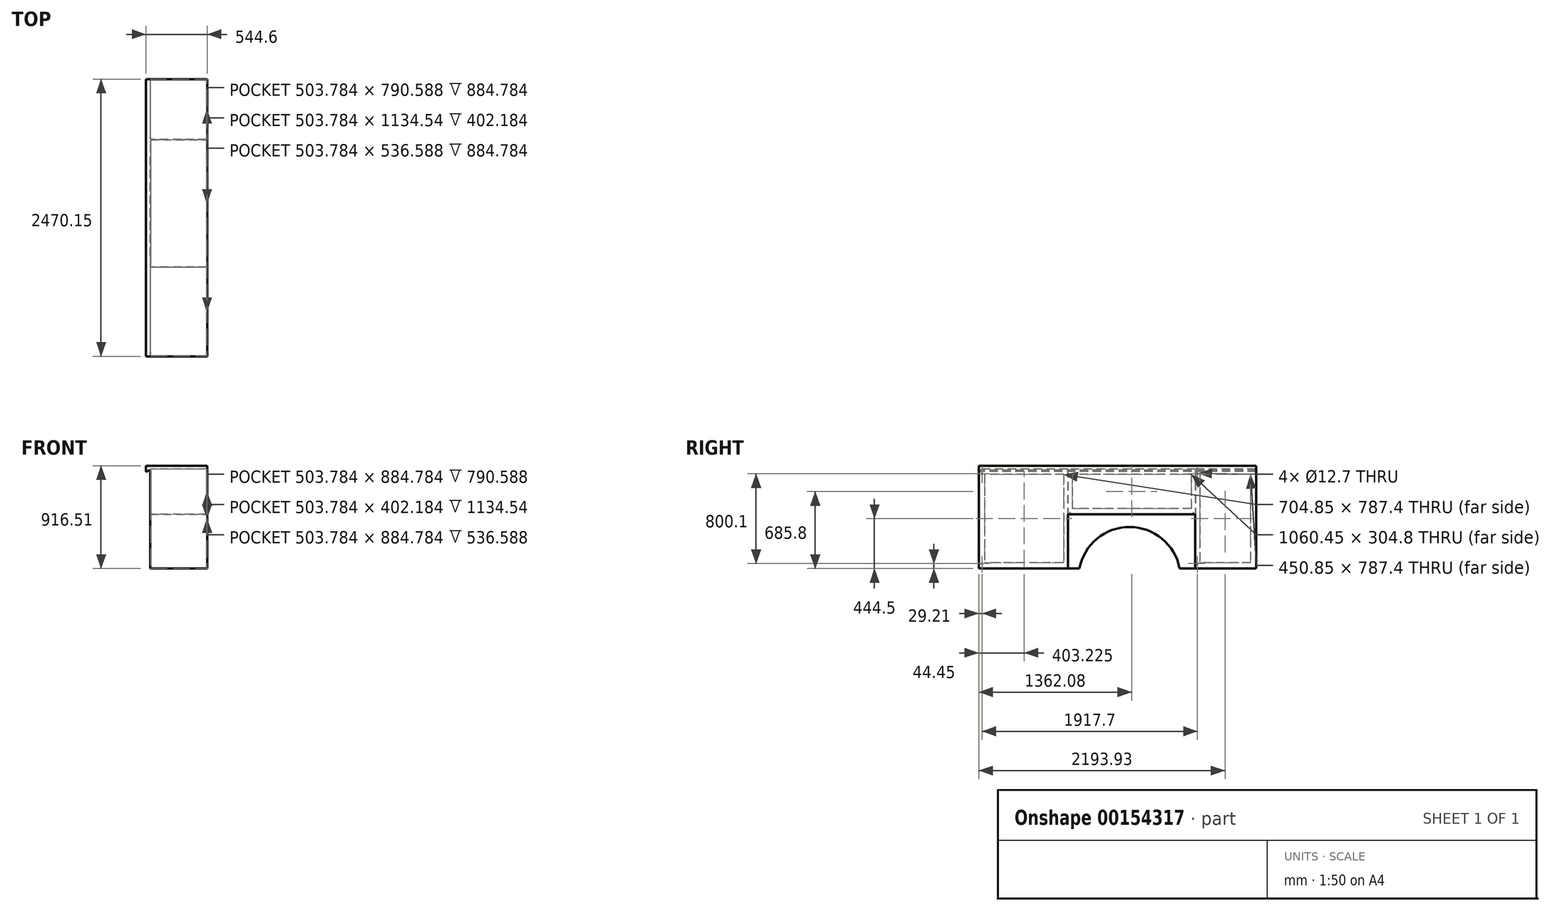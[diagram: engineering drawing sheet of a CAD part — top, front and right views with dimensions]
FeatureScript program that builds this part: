
annotation { "Feature Type Name" : "Feature", "Feature Type Description" : "" }
export const myFeature = defineFeature(function(context is Context, id is Id, definition is map)
    precondition{}
    {
        {
            var Q0;
            Q0=qCreatedBy(makeId("Front.planeOp"),FACE);
            var sketch = newSketch(context, id + "F0", { "sketchPlane" : qUnion([Q0])});
            skLineSegment(sketch, "E0.bottom", {"start": v(-254, 457.2) * mm, "end": v(254, 457.2) * mm});
            skLineSegment(sketch, "E0.top", {"start": v(-254, -457.2) * mm, "end": v(254, -457.2) * mm});
            skLineSegment(sketch, "E0.left", {"start": v(-254, 457.2) * mm, "end": v(-254, -457.2) * mm});
            skLineSegment(sketch, "E0.right", {"start": v(254, 457.2) * mm, "end": v(254, -457.2) * mm});
            skPoint(sketch, "E0.middle", {"position": v(0, 0) * mm});
            skSolve(sketch);
        }
        {
            var Q0;
            Q0 = qSketchRegion(id + "F0", true);
            var Q1;
            Q1 = qSketchRegion(id + "F2", true);
            extrude(context, id + "F1", {"entities" : qUnion([Q0, Q1]), "oppositeDirection" : true, "depth" : 2470.15 * mm});
        }
        {
            var Q0;
            Q0=makeQuery(id+"F1.opExtrude","SWEPT_FACE",FACE,{"disambiguationData":[OSD([sQuery(id+"F0.wireOp",EDGE,"E0.left")])]});
            var sketch = newSketch(context, id + "F2", { "sketchPlane" : qUnion([Q0])});
            skLineSegment(sketch, "E1", {"start": v(-1930.4, 457.2) * mm, "end": v(-1930.4, -457.2) * mm});
            skLineSegment(sketch, "E2", {"start": v(-793.75, 457.2) * mm, "end": v(-793.75, -457.2) * mm});
            skLineSegment(sketch, "E3", {"start": v(-1930.4, 25.4) * mm, "end": v(-793.75, 25.4) * mm});
            skLineSegment(sketch, "E4.bottom", {"start": v(-2419.35, 381) * mm, "end": v(-1968.5, 381) * mm});
            skLineSegment(sketch, "E4.top", {"start": v(-2419.35, -406.4) * mm, "end": v(-1968.5, -406.4) * mm});
            skLineSegment(sketch, "E4.left", {"start": v(-2419.35, 381) * mm, "end": v(-2419.35, -406.4) * mm});
            skLineSegment(sketch, "E4.right", {"start": v(-1968.5, 381) * mm, "end": v(-1968.5, -406.4) * mm});
            skLineSegment(sketch, "E5.bottom", {"start": v(-1892.3, 381) * mm, "end": v(-831.85, 381) * mm});
            skLineSegment(sketch, "E5.top", {"start": v(-1892.3, 76.2) * mm, "end": v(-831.85, 76.2) * mm});
            skLineSegment(sketch, "E5.left", {"start": v(-1892.3, 381) * mm, "end": v(-1892.3, 76.2) * mm});
            skLineSegment(sketch, "E5.right", {"start": v(-831.85, 381) * mm, "end": v(-831.85, 76.2) * mm});
            skLineSegment(sketch, "E6.bottom", {"start": v(-755.65, 381) * mm, "end": v(-50.8, 381) * mm});
            skLineSegment(sketch, "E6.top", {"start": v(-755.65, -406.4) * mm, "end": v(-50.8, -406.4) * mm});
            skLineSegment(sketch, "E6.left", {"start": v(-755.65, 381) * mm, "end": v(-755.65, -406.4) * mm});
            skLineSegment(sketch, "E6.right", {"start": v(-50.8, 381) * mm, "end": v(-50.8, -406.4) * mm});
            skSolve(sketch);
        }
        {
            var Q0;
            Q0 = qSketchRegion(id + "F2", true);
            extrude(context, id + "F3", {"entities" : qUnion([Q0]), "operationType" : NewBodyOperationType.REMOVE, "oppositeDirection" : true, "depth" : 505.9 * mm});
        }
        {
            var Q0;
            Q0=makeQuery(id+"F3.boolean.opBoolean","COPY",FACE,{"derivedFrom":makeQuery(id+"F3.opExtrude","SWEPT_FACE",FACE,{"disambiguationData":[OSD([sQuery(id+"F2.wireOp",EDGE,"E6.top")])]})});
            var sketch = newSketch(context, id + "F4", { "sketchPlane" : qUnion([Q0])});
            skLineSegment(sketch, "E7.bottom", {"start": v(251.9, 50.8) * mm, "end": v(-251.9, 50.8) * mm});
            skLineSegment(sketch, "E7.top", {"start": v(251.9, 755.65) * mm, "end": v(-251.9, 755.65) * mm});
            skLineSegment(sketch, "E7.left", {"start": v(251.9, 50.8) * mm, "end": v(251.9, 755.65) * mm});
            skLineSegment(sketch, "E7.right", {"start": v(-251.9, 50.8) * mm, "end": v(-251.9, 755.65) * mm});
            skSolve(sketch);
        }
        {
            var Q0;
            Q0 = qSketchRegion(id + "F4", true);
            extrude(context, id + "F5", {"entities" : qUnion([Q0]), "operationType" : NewBodyOperationType.REMOVE, "oppositeDirection" : true, "depth" : 48.7 * mm});
        }
        {
            var Q0;
            Q0=makeQuery(id+"F3.boolean.opBoolean","COPY",FACE,{"derivedFrom":makeQuery(id+"F3.opExtrude","SWEPT_FACE",FACE,{"disambiguationData":[OSD([sQuery(id+"F2.wireOp",EDGE,"E6.bottom")])]})});
            var sketch = newSketch(context, id + "F6", { "sketchPlane" : qUnion([Q0])});
            skLineSegment(sketch, "E8.bottom", {"start": v(251.9, -50.8) * mm, "end": v(-251.9, -50.8) * mm});
            skLineSegment(sketch, "E8.top", {"start": v(251.9, -755.65) * mm, "end": v(-251.9, -755.65) * mm});
            skLineSegment(sketch, "E8.left", {"start": v(251.9, -50.8) * mm, "end": v(251.9, -755.65) * mm});
            skLineSegment(sketch, "E8.right", {"start": v(-251.9, -50.8) * mm, "end": v(-251.9, -755.65) * mm});
            skSolve(sketch);
        }
        {
            var Q0;
            Q0 = qSketchRegion(id + "F6", true);
            extrude(context, id + "F7", {"entities" : qUnion([Q0]), "operationType" : NewBodyOperationType.REMOVE, "oppositeDirection" : true, "depth" : 48.7 * mm});
        }
        {
            var Q0;
            Q0=makeQuery(id+"F7.boolean.opBoolean","MERGE",FACE,{"derivedFrom":[makeQuery(id+"F5.boolean.opBoolean","MERGE",FACE,{"derivedFrom":[makeQuery(id+"F3.boolean.opBoolean","COPY",FACE,{"derivedFrom":makeQuery(id+"F3.opExtrude","SWEPT_FACE",FACE,{"disambiguationData":[OSD([sQuery(id+"F2.wireOp",EDGE,"E6.left")])]})}),makeQuery(id+"F5.opExtrude","SWEPT_FACE",FACE,{"disambiguationData":[OSD([sQuery(id+"F4.wireOp",EDGE,"E7.top")])]})]}),makeQuery(id+"F7.opExtrude","SWEPT_FACE",FACE,{"disambiguationData":[OSD([sQuery(id+"F6.wireOp",EDGE,"E8.top")])]})]});
            var sketch = newSketch(context, id + "F8", { "sketchPlane" : qUnion([Q0])});
            skLineSegment(sketch, "E9.bottom", {"start": v(251.9, 429.7) * mm, "end": v(-251.9, 429.7) * mm});
            skLineSegment(sketch, "E9.top", {"start": v(251.9, -455.1) * mm, "end": v(-251.9, -455.1) * mm});
            skLineSegment(sketch, "E9.left", {"start": v(251.9, 429.7) * mm, "end": v(251.9, -455.1) * mm});
            skLineSegment(sketch, "E9.right", {"start": v(-251.9, 429.7) * mm, "end": v(-251.9, -455.1) * mm});
            skSolve(sketch);
        }
        {
            var Q0;
            Q0 = qSketchRegion(id + "F8", true);
            extrude(context, id + "F9", {"entities" : qUnion([Q0]), "operationType" : NewBodyOperationType.REMOVE, "oppositeDirection" : true, "depth" : 37.05 * mm});
        }
        {
            var Q0;
            Q0=makeQuery(id+"F7.boolean.opBoolean","MERGE",FACE,{"derivedFrom":[makeQuery(id+"F5.boolean.opBoolean","MERGE",FACE,{"derivedFrom":[makeQuery(id+"F3.boolean.opBoolean","COPY",FACE,{"derivedFrom":makeQuery(id+"F3.opExtrude","SWEPT_FACE",FACE,{"disambiguationData":[OSD([sQuery(id+"F2.wireOp",EDGE,"E6.right")])]})}),makeQuery(id+"F5.opExtrude","SWEPT_FACE",FACE,{"disambiguationData":[OSD([sQuery(id+"F4.wireOp",EDGE,"E7.bottom")])]})]}),makeQuery(id+"F7.opExtrude","SWEPT_FACE",FACE,{"disambiguationData":[OSD([sQuery(id+"F6.wireOp",EDGE,"E8.bottom")])]})]});
            var sketch = newSketch(context, id + "F10", { "sketchPlane" : qUnion([Q0])});
            skLineSegment(sketch, "E10.bottom", {"start": v(-251.9, -455.1) * mm, "end": v(251.9, -455.1) * mm});
            skLineSegment(sketch, "E10.top", {"start": v(-251.9, 429.7) * mm, "end": v(251.9, 429.7) * mm});
            skLineSegment(sketch, "E10.left", {"start": v(-251.9, -455.1) * mm, "end": v(-251.9, 429.7) * mm});
            skLineSegment(sketch, "E10.right", {"start": v(251.9, -455.1) * mm, "end": v(251.9, 429.7) * mm});
            skSolve(sketch);
        }
        {
            var Q0;
            Q0 = qSketchRegion(id + "F10", true);
            extrude(context, id + "F11", {"entities" : qUnion([Q0]), "operationType" : NewBodyOperationType.REMOVE, "oppositeDirection" : true, "depth" : 48.7 * mm});
        }
        {
            var Q0;
            Q0=makeQuery(id+"F3.boolean.opBoolean","COPY",FACE,{"derivedFrom":makeQuery(id+"F3.opExtrude","SWEPT_FACE",FACE,{"disambiguationData":[OSD([sQuery(id+"F2.wireOp",EDGE,"E5.top")])]})});
            var sketch = newSketch(context, id + "F12", { "sketchPlane" : qUnion([Q0])});
            skLineSegment(sketch, "E11.bottom", {"start": v(251.9, 1892.3) * mm, "end": v(-251.9, 1892.3) * mm});
            skLineSegment(sketch, "E11.top", {"start": v(251.9, 831.85) * mm, "end": v(-251.9, 831.85) * mm});
            skLineSegment(sketch, "E11.left", {"start": v(251.9, 1892.3) * mm, "end": v(251.9, 831.85) * mm});
            skLineSegment(sketch, "E11.right", {"start": v(-251.9, 1892.3) * mm, "end": v(-251.9, 831.85) * mm});
            skSolve(sketch);
        }
        {
            var Q0;
            Q0 = qSketchRegion(id + "F12", true);
            extrude(context, id + "F13", {"entities" : qUnion([Q0]), "operationType" : NewBodyOperationType.REMOVE, "oppositeDirection" : true, "depth" : 48.7 * mm});
        }
        {
            var Q0;
            Q0=makeQuery(id+"F3.boolean.opBoolean","COPY",FACE,{"derivedFrom":makeQuery(id+"F3.opExtrude","SWEPT_FACE",FACE,{"disambiguationData":[OSD([sQuery(id+"F2.wireOp",EDGE,"E5.bottom")])]})});
            var sketch = newSketch(context, id + "F14", { "sketchPlane" : qUnion([Q0])});
            skLineSegment(sketch, "E12.bottom", {"start": v(251.9, -1892.3) * mm, "end": v(-251.9, -1892.3) * mm});
            skLineSegment(sketch, "E12.top", {"start": v(251.9, -831.85) * mm, "end": v(-251.9, -831.85) * mm});
            skLineSegment(sketch, "E12.left", {"start": v(251.9, -1892.3) * mm, "end": v(251.9, -831.85) * mm});
            skLineSegment(sketch, "E12.right", {"start": v(-251.9, -1892.3) * mm, "end": v(-251.9, -831.85) * mm});
            skSolve(sketch);
        }
        {
            var Q0;
            Q0 = qSketchRegion(id + "F14", true);
            extrude(context, id + "F15", {"entities" : qUnion([Q0]), "operationType" : NewBodyOperationType.REMOVE, "oppositeDirection" : true, "depth" : 48.7 * mm});
        }
        {
            var Q0;
            Q0=makeQuery(id+"F15.boolean.opBoolean","MERGE",FACE,{"derivedFrom":[makeQuery(id+"F13.boolean.opBoolean","MERGE",FACE,{"derivedFrom":[makeQuery(id+"F3.boolean.opBoolean","COPY",FACE,{"derivedFrom":makeQuery(id+"F3.opExtrude","SWEPT_FACE",FACE,{"disambiguationData":[OSD([sQuery(id+"F2.wireOp",EDGE,"E5.right")])]})}),makeQuery(id+"F13.opExtrude","SWEPT_FACE",FACE,{"disambiguationData":[OSD([sQuery(id+"F12.wireOp",EDGE,"E11.top")])]})]}),makeQuery(id+"F15.opExtrude","SWEPT_FACE",FACE,{"disambiguationData":[OSD([sQuery(id+"F14.wireOp",EDGE,"E12.top")])]})]});
            var sketch = newSketch(context, id + "F16", { "sketchPlane" : qUnion([Q0])});
            skLineSegment(sketch, "E13.bottom", {"start": v(-251.9, 27.5) * mm, "end": v(251.9, 27.5) * mm});
            skLineSegment(sketch, "E13.top", {"start": v(-251.9, 429.7) * mm, "end": v(251.9, 429.7) * mm});
            skLineSegment(sketch, "E13.left", {"start": v(-251.9, 27.5) * mm, "end": v(-251.9, 429.7) * mm});
            skLineSegment(sketch, "E13.right", {"start": v(251.9, 27.5) * mm, "end": v(251.9, 429.7) * mm});
            skSolve(sketch);
        }
        {
            var Q0;
            Q0 = qSketchRegion(id + "F16", true);
            extrude(context, id + "F17", {"entities" : qUnion([Q0]), "operationType" : NewBodyOperationType.REMOVE, "oppositeDirection" : true, "depth" : 37.05 * mm});
        }
        {
            var Q0;
            Q0=makeQuery(id+"F15.boolean.opBoolean","MERGE",FACE,{"derivedFrom":[makeQuery(id+"F13.boolean.opBoolean","MERGE",FACE,{"derivedFrom":[makeQuery(id+"F3.boolean.opBoolean","COPY",FACE,{"derivedFrom":makeQuery(id+"F3.opExtrude","SWEPT_FACE",FACE,{"disambiguationData":[OSD([sQuery(id+"F2.wireOp",EDGE,"E5.left")])]})}),makeQuery(id+"F13.opExtrude","SWEPT_FACE",FACE,{"disambiguationData":[OSD([sQuery(id+"F12.wireOp",EDGE,"E11.bottom")])]})]}),makeQuery(id+"F15.opExtrude","SWEPT_FACE",FACE,{"disambiguationData":[OSD([sQuery(id+"F14.wireOp",EDGE,"E12.bottom")])]})]});
            var sketch = newSketch(context, id + "F18", { "sketchPlane" : qUnion([Q0])});
            skLineSegment(sketch, "E14.bottom", {"start": v(251.9, 27.5) * mm, "end": v(-251.9, 27.5) * mm});
            skLineSegment(sketch, "E14.top", {"start": v(251.9, 429.7) * mm, "end": v(-251.9, 429.7) * mm});
            skLineSegment(sketch, "E14.left", {"start": v(251.9, 27.5) * mm, "end": v(251.9, 429.7) * mm});
            skLineSegment(sketch, "E14.right", {"start": v(-251.9, 27.5) * mm, "end": v(-251.9, 429.7) * mm});
            skSolve(sketch);
        }
        {
            var Q0;
            Q0 = qSketchRegion(id + "F18", true);
            extrude(context, id + "F19", {"entities" : qUnion([Q0]), "operationType" : NewBodyOperationType.REMOVE, "oppositeDirection" : true, "depth" : 37.05 * mm});
        }
        {
            var Q0;
            Q0=makeQuery(id+"F3.boolean.opBoolean","COPY",FACE,{"derivedFrom":makeQuery(id+"F3.opExtrude","SWEPT_FACE",FACE,{"disambiguationData":[OSD([sQuery(id+"F2.wireOp",EDGE,"E4.top")])]})});
            var sketch = newSketch(context, id + "F20", { "sketchPlane" : qUnion([Q0])});
            skLineSegment(sketch, "E15.bottom", {"start": v(251.9, 1968.5) * mm, "end": v(-251.9, 1968.5) * mm});
            skLineSegment(sketch, "E15.top", {"start": v(251.9, 2419.35) * mm, "end": v(-251.9, 2419.35) * mm});
            skLineSegment(sketch, "E15.left", {"start": v(251.9, 1968.5) * mm, "end": v(251.9, 2419.35) * mm});
            skLineSegment(sketch, "E15.right", {"start": v(-251.9, 1968.5) * mm, "end": v(-251.9, 2419.35) * mm});
            skSolve(sketch);
        }
        {
            var Q0;
            Q0 = qSketchRegion(id + "F20", true);
            extrude(context, id + "F21", {"entities" : qUnion([Q0]), "operationType" : NewBodyOperationType.REMOVE, "oppositeDirection" : true, "depth" : 48.7 * mm});
        }
        {
            var Q0;
            Q0=makeQuery(id+"F3.boolean.opBoolean","COPY",FACE,{"derivedFrom":makeQuery(id+"F3.opExtrude","SWEPT_FACE",FACE,{"disambiguationData":[OSD([sQuery(id+"F2.wireOp",EDGE,"E4.bottom")])]})});
            var sketch = newSketch(context, id + "F22", { "sketchPlane" : qUnion([Q0])});
            skLineSegment(sketch, "E16.bottom", {"start": v(251.9, -1968.5) * mm, "end": v(-251.9, -1968.5) * mm});
            skLineSegment(sketch, "E16.top", {"start": v(251.9, -2419.35) * mm, "end": v(-251.9, -2419.35) * mm});
            skLineSegment(sketch, "E16.left", {"start": v(251.9, -1968.5) * mm, "end": v(251.9, -2419.35) * mm});
            skLineSegment(sketch, "E16.right", {"start": v(-251.9, -1968.5) * mm, "end": v(-251.9, -2419.35) * mm});
            skSolve(sketch);
        }
        {
            var Q0;
            Q0 = qSketchRegion(id + "F22", true);
            extrude(context, id + "F23", {"entities" : qUnion([Q0]), "operationType" : NewBodyOperationType.REMOVE, "oppositeDirection" : true, "depth" : 48.7 * mm});
        }
        {
            var Q0;
            Q0=makeQuery(id+"F23.boolean.opBoolean","MERGE",FACE,{"derivedFrom":[makeQuery(id+"F21.boolean.opBoolean","MERGE",FACE,{"derivedFrom":[makeQuery(id+"F3.boolean.opBoolean","COPY",FACE,{"derivedFrom":makeQuery(id+"F3.opExtrude","SWEPT_FACE",FACE,{"disambiguationData":[OSD([sQuery(id+"F2.wireOp",EDGE,"E4.right")])]})}),makeQuery(id+"F21.opExtrude","SWEPT_FACE",FACE,{"disambiguationData":[OSD([sQuery(id+"F20.wireOp",EDGE,"E15.bottom")])]})]}),makeQuery(id+"F23.opExtrude","SWEPT_FACE",FACE,{"disambiguationData":[OSD([sQuery(id+"F22.wireOp",EDGE,"E16.bottom")])]})]});
            var sketch = newSketch(context, id + "F24", { "sketchPlane" : qUnion([Q0])});
            skLineSegment(sketch, "E17.bottom", {"start": v(-251.9, -455.1) * mm, "end": v(251.9, -455.1) * mm});
            skLineSegment(sketch, "E17.top", {"start": v(-251.9, 429.7) * mm, "end": v(251.9, 429.7) * mm});
            skLineSegment(sketch, "E17.left", {"start": v(-251.9, -455.1) * mm, "end": v(-251.9, 429.7) * mm});
            skLineSegment(sketch, "E17.right", {"start": v(251.9, -455.1) * mm, "end": v(251.9, 429.7) * mm});
            skSolve(sketch);
        }
        {
            var Q0;
            Q0 = qSketchRegion(id + "F24", true);
            extrude(context, id + "F25", {"entities" : qUnion([Q0]), "operationType" : NewBodyOperationType.REMOVE, "oppositeDirection" : true, "depth" : 37.05 * mm});
        }
        {
            var Q0;
            Q0=makeQuery(id+"F23.boolean.opBoolean","MERGE",FACE,{"derivedFrom":[makeQuery(id+"F21.boolean.opBoolean","MERGE",FACE,{"derivedFrom":[makeQuery(id+"F3.boolean.opBoolean","COPY",FACE,{"derivedFrom":makeQuery(id+"F3.opExtrude","SWEPT_FACE",FACE,{"disambiguationData":[OSD([sQuery(id+"F2.wireOp",EDGE,"E4.left")])]})}),makeQuery(id+"F21.opExtrude","SWEPT_FACE",FACE,{"disambiguationData":[OSD([sQuery(id+"F20.wireOp",EDGE,"E15.top")])]})]}),makeQuery(id+"F23.opExtrude","SWEPT_FACE",FACE,{"disambiguationData":[OSD([sQuery(id+"F22.wireOp",EDGE,"E16.top")])]})]});
            var sketch = newSketch(context, id + "F26", { "sketchPlane" : qUnion([Q0])});
            skLineSegment(sketch, "E18.bottom", {"start": v(251.9, -455.1) * mm, "end": v(-251.9, -455.1) * mm});
            skLineSegment(sketch, "E18.top", {"start": v(251.9, 429.7) * mm, "end": v(-251.9, 429.7) * mm});
            skLineSegment(sketch, "E18.left", {"start": v(251.9, -455.1) * mm, "end": v(251.9, 429.7) * mm});
            skLineSegment(sketch, "E18.right", {"start": v(-251.9, -455.1) * mm, "end": v(-251.9, 429.7) * mm});
            skSolve(sketch);
        }
        {
            var Q0;
            Q0 = qSketchRegion(id + "F26", true);
            extrude(context, id + "F27", {"entities" : qUnion([Q0]), "operationType" : NewBodyOperationType.REMOVE, "oppositeDirection" : true, "depth" : 48.7 * mm});
        }
        {
            var Q0;
            Q0=makeQuery(id+"F1.opExtrude","SWEPT_FACE",FACE,{"disambiguationData":[OSD([sQuery(id+"F0.wireOp",EDGE,"E0.top")])]});
            var sketch = newSketch(context, id + "F28", { "sketchPlane" : qUnion([Q0])});
            skLineSegment(sketch, "E19.bottom", {"start": v(-251.9, -1929.35) * mm, "end": v(254, -1929.35) * mm});
            skLineSegment(sketch, "E19.top", {"start": v(-251.9, -794.8) * mm, "end": v(254, -794.8) * mm});
            skLineSegment(sketch, "E19.left", {"start": v(-251.9, -1929.35) * mm, "end": v(-251.9, -794.8) * mm});
            skLineSegment(sketch, "E19.right", {"start": v(254, -1929.35) * mm, "end": v(254, -794.8) * mm});
            skSolve(sketch);
        }
        {
            var Q0;
            Q0 = qSketchRegion(id + "F28", true);
            extrude(context, id + "F29", {"entities" : qUnion([Q0]), "operationType" : NewBodyOperationType.REMOVE, "oppositeDirection" : true, "depth" : 482.6 * mm});
        }
        {
            var Q0;
            Q0=makeQuery(id+"F1.opExtrude","SWEPT_FACE",FACE,{"disambiguationData":[OSD([sQuery(id+"F0.wireOp",EDGE,"E0.left")])]});
            var sketch = newSketch(context, id + "F30", { "sketchPlane" : qUnion([Q0])});
            skArc(sketch, "E20", {"start": v(-896.4, -457.2) * mm, "mid": v(-1343.03, -86.8) * mm, "end": v(-1789.65, -457.2) * mm});
            skPoint(sketch, "E21", {"position": v(-1343.03, -86.8) * mm});
            skLineSegment(sketch, "E22", {"start": v(-1789.65, -457.2) * mm, "end": v(-896.4, -457.2) * mm});
            skSolve(sketch);
        }
        {
            var Q0;
            Q0 = qSketchRegion(id + "F30", true);
            extrude(context, id + "F31", {"entities" : qUnion([Q0]), "operationType" : NewBodyOperationType.REMOVE, "endBound" : BoundingType.THROUGH_ALL, "oppositeDirection" : true, "depth" : 25.4 * mm});
        }
        {
            var Q0;
            Q0=makeQuery(id+"F1.opExtrude","CAP_FACE",FACE,{"disambiguationData":[OSD([sQuery(id+"F0.wireOp",EDGE,"E0.bottom"),sQuery(id+"F0.wireOp",EDGE,"E0.top"),sQuery(id+"F0.wireOp",EDGE,"E0.left"),sQuery(id+"F0.wireOp",EDGE,"E0.right")])],"isStart":true});
            var sketch = newSketch(context, id + "F32", { "sketchPlane" : qUnion([Q0])});
            skLineSegment(sketch, "E23", {"start": v(-290.6, 408.5) * mm, "end": v(-290.6, 459.3) * mm});
            skLineSegment(sketch, "E24", {"start": v(-290.6, 459.3) * mm, "end": v(254, 459.3) * mm});
            skLineSegment(sketch, "E25", {"start": v(254, 459.3) * mm, "end": v(254, 457.2) * mm});
            skLineSegment(sketch, "E26", {"start": v(254, 457.2) * mm, "end": v(-254, 457.2) * mm});
            skLineSegment(sketch, "E27", {"start": v(-254, 457.2) * mm, "end": v(-254, 419.1) * mm});
            skLineSegment(sketch, "E28", {"start": v(-254, 419.1) * mm, "end": v(-290.6, 408.5) * mm});
            skSolve(sketch);
        }
        {
            var Q0;
            Q0 = qSketchRegion(id + "F32", true);
            var Q1;
            Q1=makeQuery(id+"F1.opExtrude","CAP_FACE",FACE,{"disambiguationData":[OSD([sQuery(id+"F0.wireOp",EDGE,"E0.bottom"),sQuery(id+"F0.wireOp",EDGE,"E0.top"),sQuery(id+"F0.wireOp",EDGE,"E0.left"),sQuery(id+"F0.wireOp",EDGE,"E0.right")])],"isStart":false});
            extrude(context, id + "F33", {"entities" : qUnion([Q0]), "operationType" : NewBodyOperationType.ADD, "endBound" : BoundingType.UP_TO_SURFACE, "oppositeDirection" : true, "endBoundEntityFace" : qUnion([Q1]), "depth" : 25.4 * mm});
        }
        {
            var Q0;
            Q0=makeQuery(id+"F33.opExtrude","SWEPT_EDGE",EDGE,{"disambiguationData":[OSD([sQuery(id+"F32.wireOp",EDGE,"E23"),sQuery(id+"F32.wireOp",EDGE,"E28")])]});
            fillet(context, id + "F34", {"entities" : qUnion([Q0]), "radius" : 0.5 * mm, "tangentPropagation" : true, "allowEdgeOverflow" : false});
        }
        {
            var Q0;
            Q0=makeQuery(id+"F1.opExtrude","SWEPT_FACE",FACE,{"disambiguationData":[OSD([sQuery(id+"F0.wireOp",EDGE,"E0.left")])]});
            var sketch = newSketch(context, id + "F35", { "sketchPlane" : qUnion([Q0])});
            skCircle(sketch, "E29", {"center": v(-1911.35, 38.1) * mm, "radius": 3.18 * mm});
            skLineSegment(sketch, "E30", {"start": v(-1362.08, 381) * mm, "end": v(-1362.08, 76.2) * mm});
            skCircle(sketch, "E31.MirrorC", {"center": v(-812.8, 38.1) * mm, "radius": 3.18 * mm});
            skSolve(sketch);
        }
        {
            var Q0;
            Q0 = qSketchRegion(id + "F35", true);
            var Q1;
            Q1=makeQuery(id+"F29.boolean.opBoolean","COPY",FACE,{"derivedFrom":makeQuery(id+"F29.opExtrude","SWEPT_FACE",FACE,{"disambiguationData":[OSD([sQuery(id+"F28.wireOp",EDGE,"E19.left")])]})});
            extrude(context, id + "F36", {"entities" : qUnion([Q0]), "operationType" : NewBodyOperationType.REMOVE, "endBound" : BoundingType.UP_TO_SURFACE, "oppositeDirection" : true, "endBoundEntityFace" : qUnion([Q1]), "depth" : 25.4 * mm});
        }
        {
            var Q0;
            Q0=makeQuery(id+"F1.opExtrude","SWEPT_FACE",FACE,{"disambiguationData":[OSD([sQuery(id+"F0.wireOp",EDGE,"E0.left")])]});
            var sketch = newSketch(context, id + "F37", { "sketchPlane" : qUnion([Q0])});
            skCircle(sketch, "E32", {"center": v(-29.21, 387.35) * mm, "radius": 6.35 * mm});
            skLineSegment(sketch, "E33", {"start": v(-755.65, -12.7) * mm, "end": v(-50.8, -12.7) * mm});
            skCircle(sketch, "E34.MirrorC", {"center": v(-29.2, -412.75) * mm, "radius": 6.35 * mm});
            skSolve(sketch);
        }
        {
            var Q0;
            Q0 = qSketchRegion(id + "F37", true);
            var Q1;
            Q1=makeQuery(id+"F29.boolean.opBoolean","COPY",FACE,{"derivedFrom":makeQuery(id+"F29.opExtrude","SWEPT_FACE",FACE,{"disambiguationData":[OSD([sQuery(id+"F28.wireOp",EDGE,"E19.left")])]})});
            extrude(context, id + "F38", {"entities" : qUnion([Q0]), "operationType" : NewBodyOperationType.REMOVE, "endBound" : BoundingType.UP_TO_SURFACE, "oppositeDirection" : true, "endBoundEntityFace" : qUnion([Q1]), "depth" : 25.4 * mm});
        }
        {
            var Q0;
            Q0=makeQuery(id+"F1.opExtrude","SWEPT_FACE",FACE,{"disambiguationData":[OSD([sQuery(id+"F0.wireOp",EDGE,"E0.left")])]});
            var sketch = newSketch(context, id + "F39", { "sketchPlane" : qUnion([Q0])});
            skCircle(sketch, "E35", {"center": v(-1946.9, 387.35) * mm, "radius": 6.35 * mm});
            skLineSegment(sketch, "E36", {"start": v(-2419.35, -12.7) * mm, "end": v(-1968.5, -12.7) * mm});
            skCircle(sketch, "E37.MirrorC", {"center": v(-1946.9, -412.75) * mm, "radius": 6.35 * mm});
            skSolve(sketch);
        }
        {
            var Q0;
            Q0 = qSketchRegion(id + "F39", true);
            var Q1;
            Q1=makeQuery(id+"F29.boolean.opBoolean","COPY",FACE,{"derivedFrom":makeQuery(id+"F29.opExtrude","SWEPT_FACE",FACE,{"disambiguationData":[OSD([sQuery(id+"F28.wireOp",EDGE,"E19.left")])]})});
            extrude(context, id + "F40", {"entities" : qUnion([Q0]), "operationType" : NewBodyOperationType.REMOVE, "endBound" : BoundingType.UP_TO_SURFACE, "oppositeDirection" : true, "endBoundEntityFace" : qUnion([Q1]), "depth" : 25.4 * mm});
        }
    });
